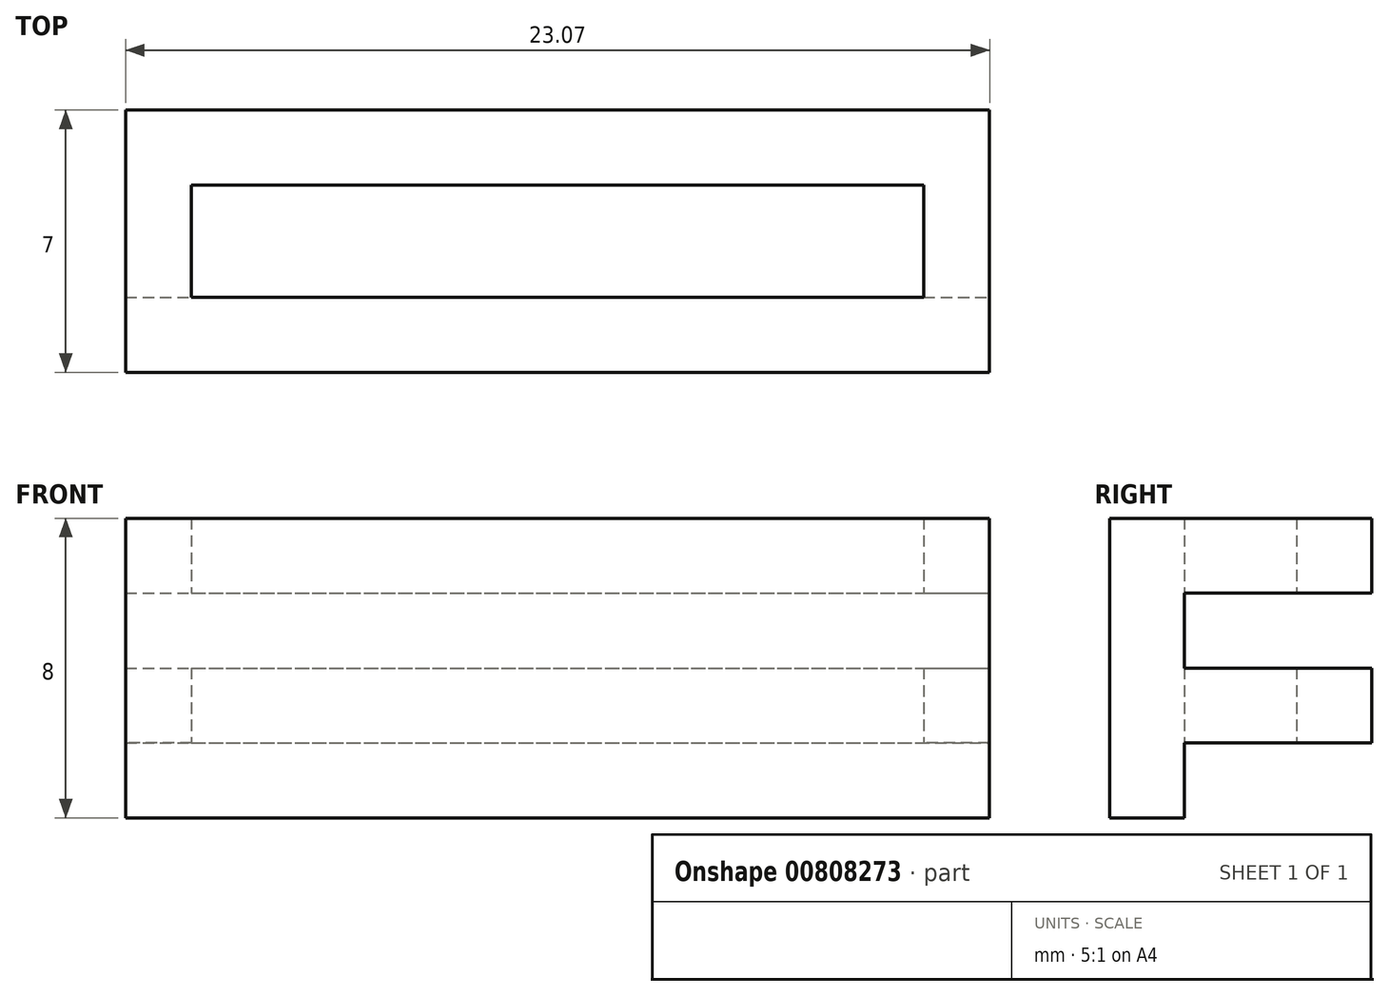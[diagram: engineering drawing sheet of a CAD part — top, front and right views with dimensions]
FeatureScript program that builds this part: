
annotation { "Feature Type Name" : "Feature", "Feature Type Description" : "" }
export const myFeature = defineFeature(function(context is Context, id is Id, definition is map)
    precondition{}
    {
        {
            var Q0;
            Q0=qCreatedBy(makeId("Top.planeOp"),FACE);
            var sketch = newSketch(context, id + "F0", { "sketchPlane" : qUnion([Q0])});
            skLineSegment(sketch, "E0.bottom", {"start": v(-8.9, 0) * mm, "end": v(14.18, 0) * mm});
            skLineSegment(sketch, "E0.top", {"start": v(-8.9, 7) * mm, "end": v(14.18, 7) * mm});
            skLineSegment(sketch, "E0.left", {"start": v(-8.9, 0) * mm, "end": v(-8.9, 7) * mm});
            skLineSegment(sketch, "E0.right", {"start": v(14.18, 0) * mm, "end": v(14.18, 7) * mm});
            skLineSegment(sketch, "E1.bottom", {"start": v(-7.13, 5) * mm, "end": v(12.42, 5) * mm});
            skLineSegment(sketch, "E1.top", {"start": v(-7.13, 2) * mm, "end": v(12.42, 2) * mm});
            skLineSegment(sketch, "E1.left", {"start": v(-7.13, 5) * mm, "end": v(-7.13, 2) * mm});
            skLineSegment(sketch, "E1.right", {"start": v(12.42, 5) * mm, "end": v(12.42, 2) * mm});
            skSolve(sketch);
        }
        {
            var Q0;
            Q0=makeQuery(id+"F0.imprint","IMPRINT",FACE,{"disambiguationData":[TD([[makeQuery(id+"F0.imprint","IMPRINT",EDGE,{"derivedFrom":sQuery(id+"F0.wireOp",EDGE,"E0.bottom")}),1.0]])]});
            extrude(context, id + "F1", {"entities" : qUnion([Q0]), "depth" : 2 * mm, "offsetDistance" : 25 * mm});
        }
        {
            var Q0;
            Q0=makeQuery(id+"F1.opExtrude","CAP_FACE",FACE,{"disambiguationData":[OSD([sQuery(id+"F0.wireOp",EDGE,"E0.bottom"),sQuery(id+"F0.wireOp",EDGE,"E0.top"),sQuery(id+"F0.wireOp",EDGE,"E0.left"),sQuery(id+"F0.wireOp",EDGE,"E0.right"),sQuery(id+"F0.wireOp",EDGE,"E1.bottom"),sQuery(id+"F0.wireOp",EDGE,"E1.top"),sQuery(id+"F0.wireOp",EDGE,"E1.left"),sQuery(id+"F0.wireOp",EDGE,"E1.right")])],"isStart":true});
            var sketch = newSketch(context, id + "F2", { "sketchPlane" : qUnion([Q0])});
            skLineSegment(sketch, "E2.bottom", {"start": v(14.18, 0) * mm, "end": v(-8.9, 0) * mm});
            skLineSegment(sketch, "E2.top", {"start": v(14.18, -2) * mm, "end": v(-8.9, -2) * mm});
            skLineSegment(sketch, "E2.left", {"start": v(14.18, 0) * mm, "end": v(14.18, -2) * mm});
            skLineSegment(sketch, "E2.right", {"start": v(-8.9, 0) * mm, "end": v(-8.9, -2) * mm});
            skSolve(sketch);
        }
        {
            var Q0;
            Q0=makeQuery(id+"F2.imprint","IMPRINT",FACE,{"disambiguationData":[TD([[makeQuery(id+"F2.imprint","IMPRINT",EDGE,{"derivedFrom":sQuery(id+"F2.wireOp",EDGE,"E2.bottom")}),-1.0]])]});
            extrude(context, id + "F3", {"entities" : qUnion([Q0]), "operationType" : NewBodyOperationType.ADD, "depth" : 2 * mm, "offsetDistance" : 25 * mm});
        }
        {
            var Q0;
            Q0=makeQuery(id+"F1.opExtrude","CAP_FACE",FACE,{"disambiguationData":[OSD([sQuery(id+"F0.wireOp",EDGE,"E0.bottom"),sQuery(id+"F0.wireOp",EDGE,"E0.top"),sQuery(id+"F0.wireOp",EDGE,"E0.left"),sQuery(id+"F0.wireOp",EDGE,"E0.right"),sQuery(id+"F0.wireOp",EDGE,"E1.bottom"),sQuery(id+"F0.wireOp",EDGE,"E1.top"),sQuery(id+"F0.wireOp",EDGE,"E1.left"),sQuery(id+"F0.wireOp",EDGE,"E1.right")])],"isStart":false});
            var sketch = newSketch(context, id + "F4", { "sketchPlane" : qUnion([Q0])});
            skLineSegment(sketch, "E3.bottom", {"start": v(-8.9, 0) * mm, "end": v(14.18, 0) * mm});
            skLineSegment(sketch, "E3.top", {"start": v(-8.9, 2) * mm, "end": v(14.18, 2) * mm});
            skLineSegment(sketch, "E3.left", {"start": v(-8.9, 0) * mm, "end": v(-8.9, 2) * mm});
            skLineSegment(sketch, "E3.right", {"start": v(14.18, 0) * mm, "end": v(14.18, 2) * mm});
            skSolve(sketch);
        }
        {
            var Q0;
            Q0=makeQuery(id+"F4.imprint","IMPRINT",FACE,{"disambiguationData":[TD([[makeQuery(id+"F4.imprint","IMPRINT",EDGE,{"derivedFrom":sQuery(id+"F4.wireOp",EDGE,"E3.bottom")}),1.0]])]});
            extrude(context, id + "F5", {"entities" : qUnion([Q0]), "operationType" : NewBodyOperationType.ADD, "depth" : 2 * mm, "offsetDistance" : 25 * mm});
        }
        {
            var Q0;
            Q0=makeQuery(id+"F5.opExtrude","CAP_FACE",FACE,{"disambiguationData":[OSD([sQuery(id+"F4.wireOp",EDGE,"E3.bottom"),sQuery(id+"F4.wireOp",EDGE,"E3.top"),sQuery(id+"F4.wireOp",EDGE,"E3.left"),sQuery(id+"F4.wireOp",EDGE,"E3.right")])],"isStart":false});
            var sketch = newSketch(context, id + "F6", { "sketchPlane" : qUnion([Q0])});
            skLineSegment(sketch, "E4.0", {"start": v(-8.9, 2) * mm, "end": v(-8.9, 7) * mm});
            skLineSegment(sketch, "E4.1", {"start": v(-8.9, 7) * mm, "end": v(14.18, 7) * mm});
            skLineSegment(sketch, "E4.2", {"start": v(-7.13, 5) * mm, "end": v(12.42, 5) * mm});
            skLineSegment(sketch, "E4.3", {"start": v(-7.13, 5) * mm, "end": v(-7.13, 2) * mm});
            skLineSegment(sketch, "E4.4", {"start": v(12.42, 5) * mm, "end": v(12.42, 2) * mm});
            skLineSegment(sketch, "E4.5", {"start": v(14.18, 2) * mm, "end": v(14.18, 7) * mm});
            skLineSegment(sketch, "E5.0", {"start": v(-8.9, 0) * mm, "end": v(-8.9, 2) * mm});
            skLineSegment(sketch, "E5.1", {"start": v(-8.9, 0) * mm, "end": v(14.18, 0) * mm});
            skLineSegment(sketch, "E5.2", {"start": v(14.18, 0) * mm, "end": v(14.18, 2) * mm});
            skLineSegment(sketch, "E6.0", {"start": v(-8.9, 2) * mm, "end": v(14.18, 2) * mm});
            skSolve(sketch);
        }
        {
            var Q0;
            Q0 = qSketchRegion(id + "F6", true);
            extrude(context, id + "F7", {"entities" : qUnion([Q0]), "operationType" : NewBodyOperationType.ADD, "depth" : 2 * mm, "offsetDistance" : 25 * mm});
        }
    });
